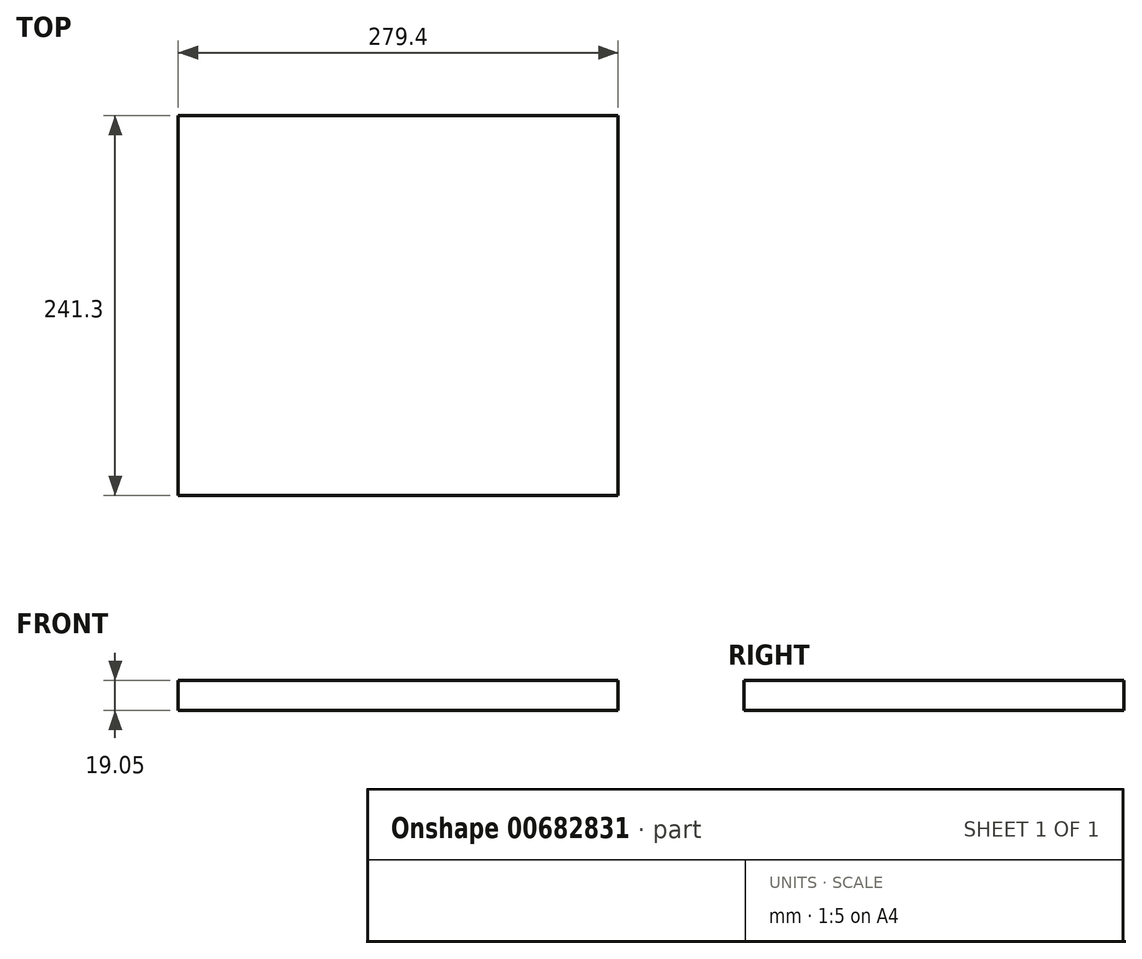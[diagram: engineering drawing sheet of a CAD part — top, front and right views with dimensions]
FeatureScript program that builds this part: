
annotation { "Feature Type Name" : "Feature", "Feature Type Description" : "" }
export const myFeature = defineFeature(function(context is Context, id is Id, definition is map)
    precondition{}
    {
        {
            var Q0;
            Q0=qCreatedBy(makeId("Top.planeOp"),FACE);
            var sketch = newSketch(context, id + "F0", { "sketchPlane" : qUnion([Q0])});
            skLineSegment(sketch, "E0.bottom", {"start": v(0, 0) * mm, "end": v(-279.4, 0) * mm});
            skLineSegment(sketch, "E0.top", {"start": v(0, 241.3) * mm, "end": v(-279.4, 241.3) * mm});
            skLineSegment(sketch, "E0.left", {"start": v(0, 0) * mm, "end": v(0, 241.3) * mm});
            skLineSegment(sketch, "E0.right", {"start": v(-279.4, 0) * mm, "end": v(-279.4, 241.3) * mm});
            skSolve(sketch);
        }
        {
            var Q0;
            Q0=makeQuery(id+"F0.imprint","IMPRINT",FACE,{"disambiguationData":[TD([[makeQuery(id+"F0.imprint","IMPRINT",EDGE,{"derivedFrom":sQuery(id+"F0.wireOp",EDGE,"E0.bottom")}),-1.0]])]});
            extrude(context, id + "F1", {"entities" : qUnion([Q0]), "depth" : 19.05 * mm, "offsetDistance" : 25.4 * mm});
        }
    });
